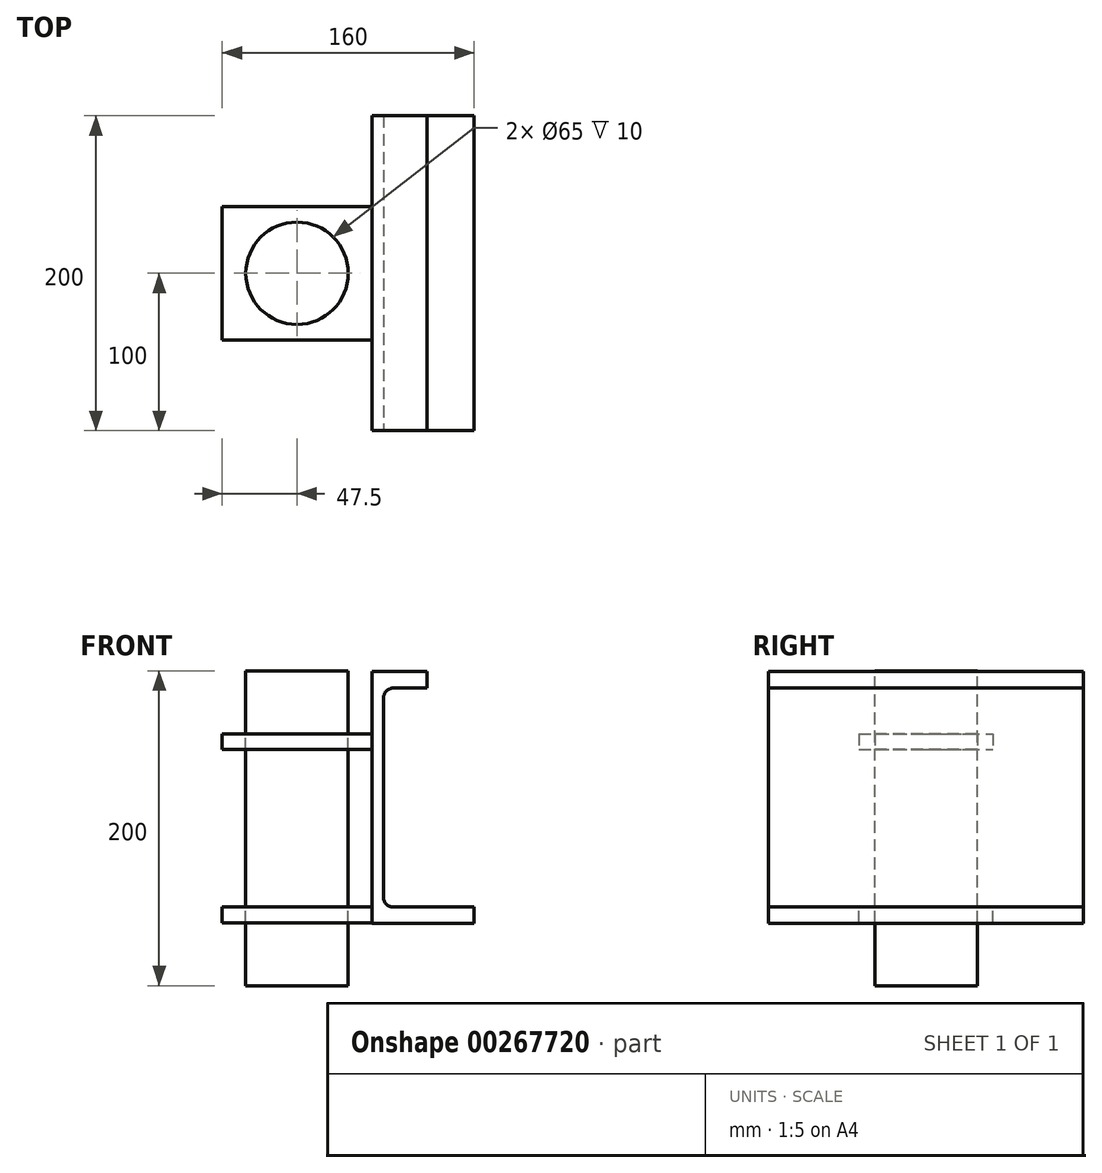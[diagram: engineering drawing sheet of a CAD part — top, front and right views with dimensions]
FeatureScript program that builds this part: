
annotation { "Feature Type Name" : "Feature", "Feature Type Description" : "" }
export const myFeature = defineFeature(function(context is Context, id is Id, definition is map)
    precondition{}
    {
        {
            var Q0;
            Q0=qCreatedBy(makeId("Front.planeOp"),FACE);
            var sketch = newSketch(context, id + "F0", { "sketchPlane" : qUnion([Q0])});
            skLineSegment(sketch, "E0.bottom", {"start": v(2.5, 80) * mm, "end": v(-32.5, 80) * mm});
            skLineSegment(sketch, "E0.top", {"start": v(32.5, -80) * mm, "end": v(-32.5, -80) * mm});
            skLineSegment(sketch, "E0.right", {"start": v(-32.5, 80) * mm, "end": v(-32.5, -80) * mm});
            skPoint(sketch, "E0.middle", {"position": v(0, 0) * mm});
            skLineSegment(sketch, "E1.0", {"start": v(2.5, 69.5) * mm, "end": v(-19, 69.5) * mm});
            skLineSegment(sketch, "E2.0", {"start": v(32.5, -69.5) * mm, "end": v(-19, -69.5) * mm});
            skLineSegment(sketch, "E3.0", {"start": v(-25, 63.5) * mm, "end": v(-25, -63.5) * mm});
            skArc(sketch, "E4.filletArc", {"start": v(-19, 69.5) * mm, "mid": v(-23.24, 67.74) * mm, "end": v(-25, 63.5) * mm});
            skArc(sketch, "E5.filletArc", {"start": v(-25, -63.5) * mm, "mid": v(-23.24, -67.74) * mm, "end": v(-19, -69.5) * mm});
            skLineSegment(sketch, "E6.trimOffspring", {"start": v(32.5, -69.5) * mm, "end": v(32.5, -80) * mm});
            skLineSegment(sketch, "E7", {"start": v(2.5, 80) * mm, "end": v(2.5, 69.5) * mm});
            skPoint(sketch, "E0.left.start.orphan", {"position": v(32.5, 80) * mm});
            skLineSegment(sketch, "E8.bottom", {"start": v(-32.5, 80) * mm, "end": v(-24.5, 80) * mm});
            skLineSegment(sketch, "E8.top", {"start": v(-32.5, 170) * mm, "end": v(-24.5, 170) * mm});
            skLineSegment(sketch, "E8.left", {"start": v(-32.5, 80) * mm, "end": v(-32.5, 170) * mm});
            skLineSegment(sketch, "E8.right", {"start": v(-24.5, 80) * mm, "end": v(-24.5, 170) * mm});
            skSolve(sketch);
        }
        {
            var Q0;
            {var subQ3=sQuery(id+"F0.wireOp",EDGE,"E0.bottom");Q0=makeQuery(id+"F0.imprint","IMPRINT",FACE,{"disambiguationData":[TD([[makeQuery(id+"F0.imprint","IMPRINT",EDGE,{"derivedFrom":subQ3}),1.0]])]});}
            var Q1;
            Q1=makeQuery(id+"F0.imprint","IMPRINT",FACE,{"disambiguationData":[TD([[makeQuery(id+"F0.imprint","IMPRINT",EDGE,{"derivedFrom":sQuery(id+"F0.wireOp",EDGE,"E8.bottom")}),1.0]])]});
            extrude(context, id + "F1", {"entities" : qUnion([Q0, Q1]), "oppositeDirection" : true, "depth" : 200 * mm});
        }
        {
            var Q0;
            Q0=makeQuery(id+"F1.opExtrude","SWEPT_FACE",FACE,{"disambiguationData":[OSD([sQuery(id+"F0.wireOp",EDGE,"E2.0")])]});
            cPlane(context, id + "F2", {"entities" : qUnion([Q0]), "cplaneType" : CPlaneType.OFFSET, "offset" : 0 * mm, "width" : 150 * mm, "height" : 150 * mm});
        }
        {
            var Q0;
            Q0=qCreatedBy(id+"F2.planeOp",FACE);
            var sketch = newSketch(context, id + "F3", { "sketchPlane" : qUnion([Q0])});
            skCircle(sketch, "E9", {"center": v(-80, 100) * mm, "radius": 32.5 * mm});
            skLineSegment(sketch, "E10.bottom", {"start": v(-127.5, 57.5) * mm, "end": v(-32.5, 57.5) * mm});
            skLineSegment(sketch, "E10.top", {"start": v(-127.5, 142.5) * mm, "end": v(-32.5, 142.5) * mm});
            skLineSegment(sketch, "E10.left", {"start": v(-127.5, 57.5) * mm, "end": v(-127.5, 142.5) * mm});
            skLineSegment(sketch, "E10.right", {"start": v(-32.5, 57.5) * mm, "end": v(-32.5, 142.5) * mm});
            skSolve(sketch);
        }
        {
            var Q0;
            Q0 = qSketchRegion(id + "F3", true);
            extrude(context, id + "F4", {"entities" : qUnion([Q0]), "operationType" : NewBodyOperationType.ADD, "oppositeDirection" : true, "depth" : 10 * mm});
        }
        {
            var Q0;
            Q0=makeQuery(id+"F4.opExtrude","CAP_FACE",FACE,{"disambiguationData":[OSD([sQuery(id+"F3.wireOp",EDGE,"E9"),sQuery(id+"F3.wireOp",EDGE,"E10.bottom"),sQuery(id+"F3.wireOp",EDGE,"E10.top"),sQuery(id+"F3.wireOp",EDGE,"E10.left"),sQuery(id+"F3.wireOp",EDGE,"E10.right")])],"isStart":true});
            cPlane(context, id + "F5", {"entities" : qUnion([Q0]), "cplaneType" : CPlaneType.OFFSET, "offset" : 100 * mm, "width" : 150 * mm, "height" : 150 * mm});
        }
        {
            var Q0;
            Q0=qCreatedBy(id+"F5.planeOp",FACE);
            var sketch = newSketch(context, id + "F6", { "sketchPlane" : qUnion([Q0])});
            skCircle(sketch, "E11", {"center": v(-80, 100) * mm, "radius": 32.5 * mm});
            skLineSegment(sketch, "E12.bottom", {"start": v(-127.5, 57.5) * mm, "end": v(-32.5, 57.5) * mm});
            skLineSegment(sketch, "E12.top", {"start": v(-127.5, 142.5) * mm, "end": v(-32.5, 142.5) * mm});
            skLineSegment(sketch, "E12.left", {"start": v(-127.5, 57.5) * mm, "end": v(-127.5, 142.5) * mm});
            skLineSegment(sketch, "E12.right", {"start": v(-32.5, 57.5) * mm, "end": v(-32.5, 142.5) * mm});
            skSolve(sketch);
        }
        {
            var Q0;
            Q0=makeQuery(id+"F6.imprint","IMPRINT",FACE,{"disambiguationData":[TD([[makeQuery(id+"F6.imprint","IMPRINT",EDGE,{"derivedFrom":sQuery(id+"F6.wireOp",EDGE,"E11")}),-1.0]])]});
            extrude(context, id + "F7", {"entities" : qUnion([Q0]), "operationType" : NewBodyOperationType.ADD, "depth" : 10 * mm});
        }
        {
            var Q0;
            Q0=makeQuery(id+"F7.opExtrude","CAP_FACE",FACE,{"disambiguationData":[OSD([sQuery(id+"F6.wireOp",EDGE,"E11"),sQuery(id+"F6.wireOp",EDGE,"E12.bottom"),sQuery(id+"F6.wireOp",EDGE,"E12.top"),sQuery(id+"F6.wireOp",EDGE,"E12.left"),sQuery(id+"F6.wireOp",EDGE,"E12.right")])],"isStart":false});
            cPlane(context, id + "F8", {"entities" : qUnion([Q0]), "cplaneType" : CPlaneType.OFFSET, "offset" : 40 * mm, "width" : 150 * mm, "height" : 150 * mm});
        }
        {
            var Q0;
            Q0=qCreatedBy(id+"F8.planeOp",FACE);
            var sketch = newSketch(context, id + "F9", { "sketchPlane" : qUnion([Q0])});
            skCircle(sketch, "E13", {"center": v(-80, 100) * mm, "radius": 32.5 * mm});
            skPoint(sketch, "E14.top.end.orphan", {"position": v(-42.5, 142.5) * mm});
            skPoint(sketch, "E14.bottom.end.orphan", {"position": v(-42.5, 57.5) * mm});
            skPoint(sketch, "E14.left.end.orphan", {"position": v(-117.5, 142.5) * mm});
            skPoint(sketch, "E14.left.start.orphan", {"position": v(-117.5, 57.5) * mm});
            skSolve(sketch);
        }
        {
            var Q0;
            Q0 = qSketchRegion(id + "F9", true);
            extrude(context, id + "F10", {"entities" : qUnion([Q0]), "oppositeDirection" : true, "depth" : 200 * mm});
        }
    });
